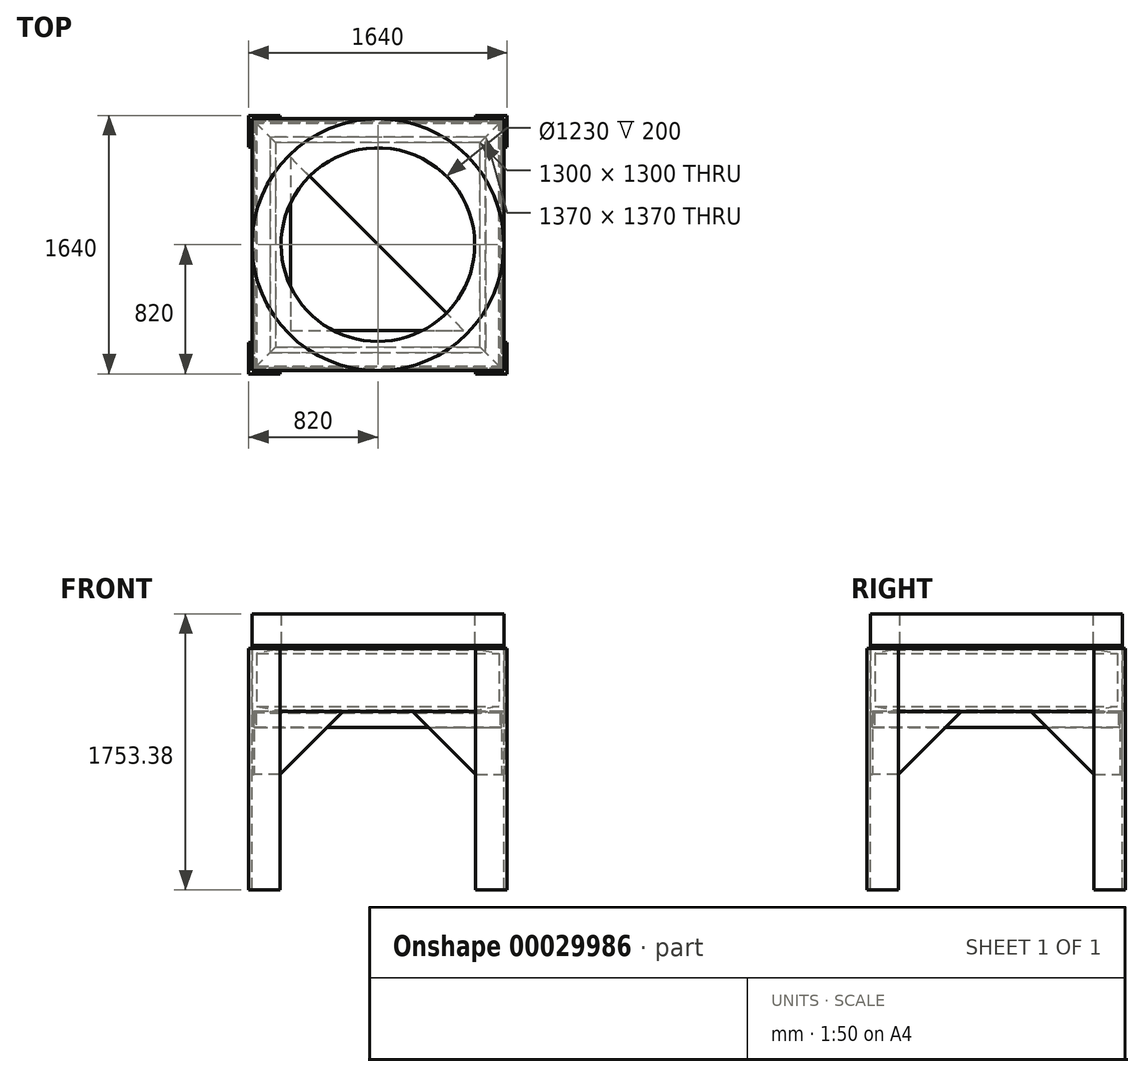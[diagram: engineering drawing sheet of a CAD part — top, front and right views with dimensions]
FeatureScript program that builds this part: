
annotation { "Feature Type Name" : "Feature", "Feature Type Description" : "" }
export const myFeature = defineFeature(function(context is Context, id is Id, definition is map)
    precondition{}
    {
        {
            var Q0;
            Q0=qCreatedBy(makeId("Top.planeOp"),FACE);
            var sketch = newSketch(context, id + "F0", { "sketchPlane" : qUnion([Q0])});
            skLineSegment(sketch, "E0.rect.bottom", {"start": v(800, -800) * mm, "end": v(-800, -800) * mm});
            skLineSegment(sketch, "E0.rect.top", {"start": v(800, 800) * mm, "end": v(-800, 800) * mm});
            skLineSegment(sketch, "E0.rect.left", {"start": v(800, -800) * mm, "end": v(800, 800) * mm});
            skLineSegment(sketch, "E0.rect.right", {"start": v(-800, -800) * mm, "end": v(-800, 800) * mm});
            skPoint(sketch, "E0.rect.middle", {"position": v(0, 0) * mm});
            skSolve(sketch);
        }
        {
            var Q0;
            Q0=qCreatedBy(makeId("Front.planeOp"),FACE);
            var sketch = newSketch(context, id + "F1", { "sketchPlane" : qUnion([Q0])});
            skLineSegment(sketch, "E1", {"start": v(-650, 200) * mm, "end": v(-800, 200) * mm});
            skLineSegment(sketch, "E2", {"start": v(-800, 200) * mm, "end": v(-800, -200) * mm});
            skLineSegment(sketch, "E3", {"start": v(-800, -200) * mm, "end": v(-650, -200) * mm});
            skLineSegment(sketch, "E4", {"start": v(-650, -200) * mm, "end": v(-650, -190) * mm});
            skLineSegment(sketch, "E5", {"start": v(-650, -190) * mm, "end": v(-770, -168.84) * mm});
            skLineSegment(sketch, "E6", {"start": v(-770, -168.84) * mm, "end": v(-770, 168.84) * mm});
            skLineSegment(sketch, "E7", {"start": v(-770, 168.84) * mm, "end": v(-650, 190) * mm});
            skLineSegment(sketch, "E8", {"start": v(-650, 190) * mm, "end": v(-650, 200) * mm});
            skLineSegment(sketch, "E9", {"start": v(0, 0) * mm, "end": v(-1109.35, 0) * mm, "construction": true});
            skSolve(sketch);
        }
        {
            var Q0;
            Q0=makeQuery(id+"F1.imprint","IMPRINT",FACE,{"disambiguationData":[TD([[makeQuery(id+"F1.imprint","IMPRINT",EDGE,{"derivedFrom":sQuery(id+"F1.wireOp",EDGE,"E1")}),1.0]])]});
            var Q1;
            Q1=sQuery(id+"F0.wireOp",EDGE,"E0.rect.right");
            var Q2;
            Q2=sQuery(id+"F0.wireOp",EDGE,"E0.rect.bottom");
            var Q3;
            Q3=sQuery(id+"F0.wireOp",EDGE,"E0.rect.left");
            var Q4;
            Q4=sQuery(id+"F0.wireOp",EDGE,"E0.rect.top");
            sweep(context, id + "F2", {"profiles" : qUnion([Q0]), "path" : qUnion([Q1, Q2, Q3, Q4])});
        }
        {
            var Q0;
            Q0=makeQuery(id+"F2.opSweep","SWEPT_FACE",FACE,{"disambiguationData":[OSD([sQuery(id+"F0.wireOp",EDGE,"E0.rect.right"),sQuery(id+"F1.wireOp",EDGE,"E1")])]});
            var sketch = newSketch(context, id + "F3", { "sketchPlane" : qUnion([Q0])});
            skLineSegment(sketch, "E10", {"start": v(-800, 800) * mm, "end": v(-800, 620) * mm});
            skLineSegment(sketch, "E11", {"start": v(-800, 800) * mm, "end": v(-620, 800) * mm});
            skLineSegment(sketch, "E12", {"start": v(-620, 800) * mm, "end": v(-620, 820) * mm});
            skLineSegment(sketch, "E13", {"start": v(-620, 820) * mm, "end": v(-820, 820) * mm});
            skLineSegment(sketch, "E14", {"start": v(-820, 820) * mm, "end": v(-820, 620) * mm});
            skLineSegment(sketch, "E15", {"start": v(-820, 620) * mm, "end": v(-800, 620) * mm});
            skLineSegment(sketch, "E16", {"start": v(0, 0) * mm, "end": v(0, 1155.08) * mm, "construction": true});
            skLineSegment(sketch, "E17.MirrorCS", {"start": v(800, 800) * mm, "end": v(800, 620) * mm});
            skLineSegment(sketch, "E18.MirrorCS", {"start": v(800, 800) * mm, "end": v(620, 800) * mm});
            skLineSegment(sketch, "E19.MirrorCS", {"start": v(620, 800) * mm, "end": v(620, 820) * mm});
            skLineSegment(sketch, "E20.MirrorCS", {"start": v(620, 820) * mm, "end": v(820, 820) * mm});
            skLineSegment(sketch, "E21.MirrorCS", {"start": v(820, 820) * mm, "end": v(820, 620) * mm});
            skLineSegment(sketch, "E22.MirrorCS", {"start": v(820, 620) * mm, "end": v(800, 620) * mm});
            skSolve(sketch);
        }
        {
            var Q0;
            Q0 = qSketchRegion(id + "F3", true);
            extrude(context, id + "F4", {"entities" : qUnion([Q0]), "oppositeDirection" : true, "depth" : 1533.38 * mm});
        }
        {
            var Q0;
            Q0=makeQuery(id+"F4.opExtrude","SWEPT_BODY",BODY,{"disambiguationData":[OSD([sQuery(id+"F3.wireOp",EDGE,"E17.MirrorCS"),sQuery(id+"F3.wireOp",EDGE,"E18.MirrorCS"),sQuery(id+"F3.wireOp",EDGE,"E19.MirrorCS"),sQuery(id+"F3.wireOp",EDGE,"E20.MirrorCS"),sQuery(id+"F3.wireOp",EDGE,"E21.MirrorCS"),sQuery(id+"F3.wireOp",EDGE,"E22.MirrorCS")])]});
            var Q1;
            Q1=makeQuery(id+"F4.opExtrude","SWEPT_BODY",BODY,{"disambiguationData":[OSD([sQuery(id+"F3.wireOp",EDGE,"E10"),sQuery(id+"F3.wireOp",EDGE,"E11"),sQuery(id+"F3.wireOp",EDGE,"E12"),sQuery(id+"F3.wireOp",EDGE,"E13"),sQuery(id+"F3.wireOp",EDGE,"E14"),sQuery(id+"F3.wireOp",EDGE,"E15")])]});
            var Q2;
            Q2=qCreatedBy(makeId("Front.planeOp"),FACE);
            mirror(context, id + "F5", {"entities" : qUnion([Q0, Q1]), "mirrorPlane" : qUnion([Q2])});
        }
        {
            var Q0;
            Q0=makeQuery(id+"F2.opSweep","SWEPT_FACE",FACE,{"disambiguationData":[OSD([sQuery(id+"F0.wireOp",EDGE,"E0.rect.right"),sQuery(id+"F1.wireOp",EDGE,"E1")])]});
            var sketch = newSketch(context, id + "F6", { "sketchPlane" : qUnion([Q0])});
            skLineSegment(sketch, "E23.bottom", {"start": v(-800, 800) * mm, "end": v(800, 800) * mm});
            skLineSegment(sketch, "E23.top", {"start": v(-800, -800) * mm, "end": v(800, -800) * mm});
            skLineSegment(sketch, "E23.left", {"start": v(-800, 800) * mm, "end": v(-800, -800) * mm});
            skLineSegment(sketch, "E23.right", {"start": v(800, 800) * mm, "end": v(800, -800) * mm});
            skLineSegment(sketch, "E24", {"start": v(-555, 555) * mm, "end": v(-555, -545) * mm});
            skLineSegment(sketch, "E25", {"start": v(-555, -545) * mm, "end": v(545, -545) * mm});
            skLineSegment(sketch, "E26", {"start": v(545, -545) * mm, "end": v(-555, 555) * mm});
            skSolve(sketch);
        }
        {
            var Q0;
            Q0 = qSketchRegion(id + "F6", true);
            extrude(context, id + "F7", {"entities" : qUnion([Q0]), "depth" : 20 * mm});
        }
        {
            var Q0;
            Q0=makeQuery(id+"F7.opExtrude","CAP_FACE",FACE,{"disambiguationData":[OSD([sQuery(id+"F6.wireOp",EDGE,"E23.bottom"),sQuery(id+"F6.wireOp",EDGE,"E23.top"),sQuery(id+"F6.wireOp",EDGE,"E23.left"),sQuery(id+"F6.wireOp",EDGE,"E23.right"),sQuery(id+"F6.wireOp",EDGE,"E24"),sQuery(id+"F6.wireOp",EDGE,"E25"),sQuery(id+"F6.wireOp",EDGE,"E26")])],"isStart":false});
            var sketch = newSketch(context, id + "F8", { "sketchPlane" : qUnion([Q0])});
            skCircle(sketch, "E27", {"center": v(0, 0) * mm, "radius": 800 * mm});
            skCircle(sketch, "E28", {"center": v(0, 0) * mm, "radius": 615 * mm});
            skSolve(sketch);
        }
        {
            var Q0;
            Q0 = qSketchRegion(id + "F8", true);
            extrude(context, id + "F9", {"entities" : qUnion([Q0]), "operationType" : NewBodyOperationType.ADD, "depth" : 200 * mm});
        }
        {
            var Q0;
            Q0=makeQuery(id+"F2.opSweep","SWEPT_FACE",FACE,{"disambiguationData":[OSD([sQuery(id+"F0.wireOp",EDGE,"E0.rect.right"),sQuery(id+"F1.wireOp",EDGE,"E3")])]});
            var sketch = newSketch(context, id + "F10", { "sketchPlane" : qUnion([Q0])});
            skLineSegment(sketch, "E29.rect.bottom", {"start": v(785, -785) * mm, "end": v(-785, -785) * mm});
            skLineSegment(sketch, "E29.rect.top", {"start": v(785, 785) * mm, "end": v(-785, 785) * mm});
            skLineSegment(sketch, "E29.rect.left", {"start": v(785, -785) * mm, "end": v(785, 785) * mm});
            skLineSegment(sketch, "E29.rect.right", {"start": v(-785, -785) * mm, "end": v(-785, 785) * mm});
            skPoint(sketch, "E29.rect.middle", {"position": v(0, 0) * mm});
            skSolve(sketch);
        }
        {
            var Q0;
            Q0=qCreatedBy(makeId("Front.planeOp"),FACE);
            var sketch = newSketch(context, id + "F11", { "sketchPlane" : qUnion([Q0])});
            skLineSegment(sketch, "E30", {"start": v(-785, -300) * mm, "end": v(-785, -200) * mm});
            skLineSegment(sketch, "E31", {"start": v(-785, -200) * mm, "end": v(-685, -200) * mm});
            skLineSegment(sketch, "E32", {"start": v(-685, -200) * mm, "end": v(-685, -210) * mm});
            skLineSegment(sketch, "E33", {"start": v(-685, -210) * mm, "end": v(-775, -210) * mm});
            skLineSegment(sketch, "E34", {"start": v(-775, -210) * mm, "end": v(-775, -300) * mm});
            skLineSegment(sketch, "E35", {"start": v(-775, -300) * mm, "end": v(-785, -300) * mm});
            skSolve(sketch);
        }
        {
            var Q0;
            Q0=makeQuery(id+"F11.imprint","IMPRINT",FACE,{"disambiguationData":[TD([[makeQuery(id+"F11.imprint","IMPRINT",EDGE,{"derivedFrom":sQuery(id+"F11.wireOp",EDGE,"E30")}),-1.0]])]});
            var Q1;
            Q1=sQuery(id+"F10.wireOp",EDGE,"E29.rect.right");
            var Q2;
            Q2=sQuery(id+"F10.wireOp",EDGE,"E29.rect.top");
            var Q3;
            Q3=sQuery(id+"F10.wireOp",EDGE,"E29.rect.left");
            var Q4;
            Q4=sQuery(id+"F10.wireOp",EDGE,"E29.rect.bottom");
            sweep(context, id + "F12", {"profiles" : qUnion([Q0]), "path" : qUnion([Q1, Q2, Q3, Q4])});
        }
        {
            var Q0;
            Q0=makeQuery(id+"F12.opSweep","SWEPT_FACE",FACE,{"disambiguationData":[OSD([sQuery(id+"F10.wireOp",EDGE,"E29.rect.top"),sQuery(id+"F11.wireOp",EDGE,"E30")])]});
            var sketch = newSketch(context, id + "F13", { "sketchPlane" : qUnion([Q0])});
            skLineSegment(sketch, "E36", {"start": v(-800, -200) * mm, "end": v(-220, -200) * mm});
            skLineSegment(sketch, "E37", {"start": v(-220, -200) * mm, "end": v(-620, -600) * mm});
            skLineSegment(sketch, "E38", {"start": v(-800, -600) * mm, "end": v(-800, -200) * mm});
            skPoint(sketch, "E39", {"position": v(-620, -600) * mm});
            skLineSegment(sketch, "E40", {"start": v(-620, -600) * mm, "end": v(-800, -600) * mm});
            skSolve(sketch);
        }
        {
            var Q0;
            Q0 = qSketchRegion(id + "F13", true);
            var Q1;
            Q1=makeQuery(id+"F2.opSweep","SWEPT_FACE",FACE,{"disambiguationData":[OSD([sQuery(id+"F0.wireOp",EDGE,"E0.rect.bottom"),sQuery(id+"F1.wireOp",EDGE,"E2")])]});
            extrude(context, id + "F14", {"entities" : qUnion([Q0]), "endBound" : BoundingType.UP_TO_SURFACE, "endBoundEntityFace" : qUnion([Q1]), "depth" : 25 * mm});
        }
        {
            var Q0;
            Q0=makeQuery(id+"F14.opExtrude","SWEPT_BODY",BODY,{"disambiguationData":[OSD([sQuery(id+"F13.wireOp",EDGE,"E36"),sQuery(id+"F13.wireOp",EDGE,"E37"),sQuery(id+"F13.wireOp",EDGE,"E38"),sQuery(id+"F13.wireOp",EDGE,"E40")])]});
            var Q1;
            Q1=qCreatedBy(makeId("Right.planeOp"),FACE);
            mirror(context, id + "F15", {"entities" : qUnion([Q0]), "mirrorPlane" : qUnion([Q1])});
        }
        {
            var Q0;
            Q0=makeQuery(id+"F14.opExtrude","SWEPT_BODY",BODY,{"disambiguationData":[OSD([sQuery(id+"F13.wireOp",EDGE,"E36"),sQuery(id+"F13.wireOp",EDGE,"E37"),sQuery(id+"F13.wireOp",EDGE,"E38"),sQuery(id+"F13.wireOp",EDGE,"E40")])]});
            var Q1;
            Q1=makeQuery(id+"F15.opPattern","COPY",BODY,{"derivedFrom":makeQuery(id+"F14.opExtrude","SWEPT_BODY",BODY,{"disambiguationData":[OSD([sQuery(id+"F13.wireOp",EDGE,"E36"),sQuery(id+"F13.wireOp",EDGE,"E37"),sQuery(id+"F13.wireOp",EDGE,"E38"),sQuery(id+"F13.wireOp",EDGE,"E40")])]}),"instanceName":"1"});
            var Q2;
            Q2=qCreatedBy(makeId("Front.planeOp"),FACE);
            mirror(context, id + "F16", {"entities" : qUnion([Q0, Q1]), "mirrorPlane" : qUnion([Q2])});
        }
        {
            var Q0;
            Q0=makeQuery(id+"F12.opSweep","SWEPT_FACE",FACE,{"disambiguationData":[OSD([sQuery(id+"F10.wireOp",EDGE,"E29.rect.right"),sQuery(id+"F11.wireOp",EDGE,"E30")])]});
            var sketch = newSketch(context, id + "F17", { "sketchPlane" : qUnion([Q0])});
            skLineSegment(sketch, "E41", {"start": v(-800, -200) * mm, "end": v(-220, -200) * mm});
            skLineSegment(sketch, "E42", {"start": v(-220, -200) * mm, "end": v(-620, -600) * mm});
            skLineSegment(sketch, "E43", {"start": v(-620, -600) * mm, "end": v(-800, -600) * mm});
            skLineSegment(sketch, "E44", {"start": v(-800, -600) * mm, "end": v(-800, -200) * mm});
            skSolve(sketch);
        }
        {
            var Q0;
            Q0 = qSketchRegion(id + "F17", true);
            var Q1;
            Q1=makeQuery(id+"F4.opExtrude","SWEPT_FACE",FACE,{"disambiguationData":[OSD([sQuery(id+"F3.wireOp",EDGE,"E10")])]});
            extrude(context, id + "F18", {"entities" : qUnion([Q0]), "endBound" : BoundingType.UP_TO_SURFACE, "endBoundEntityFace" : qUnion([Q1]), "depth" : 25 * mm});
        }
        {
            var Q0;
            Q0=makeQuery(id+"F18.opExtrude","SWEPT_BODY",BODY,{"disambiguationData":[OSD([sQuery(id+"F17.wireOp",EDGE,"E41"),sQuery(id+"F17.wireOp",EDGE,"E42"),sQuery(id+"F17.wireOp",EDGE,"E43"),sQuery(id+"F17.wireOp",EDGE,"E44")])]});
            var Q1;
            Q1=qCreatedBy(makeId("Front.planeOp"),FACE);
            mirror(context, id + "F19", {"entities" : qUnion([Q0]), "mirrorPlane" : qUnion([Q1])});
        }
        {
            var Q0;
            Q0=makeQuery(id+"F18.opExtrude","SWEPT_BODY",BODY,{"disambiguationData":[OSD([sQuery(id+"F17.wireOp",EDGE,"E41"),sQuery(id+"F17.wireOp",EDGE,"E42"),sQuery(id+"F17.wireOp",EDGE,"E43"),sQuery(id+"F17.wireOp",EDGE,"E44")])]});
            var Q1;
            Q1=makeQuery(id+"F19.opPattern","COPY",BODY,{"derivedFrom":makeQuery(id+"F18.opExtrude","SWEPT_BODY",BODY,{"disambiguationData":[OSD([sQuery(id+"F17.wireOp",EDGE,"E41"),sQuery(id+"F17.wireOp",EDGE,"E42"),sQuery(id+"F17.wireOp",EDGE,"E43"),sQuery(id+"F17.wireOp",EDGE,"E44")])]}),"instanceName":"1"});
            var Q2;
            Q2=qCreatedBy(makeId("Right.planeOp"),FACE);
            mirror(context, id + "F20", {"entities" : qUnion([Q0, Q1]), "mirrorPlane" : qUnion([Q2])});
        }
        {
            var Q0;
            Q0=qCreatedBy(makeId("Right.planeOp"),FACE);
            var sketch = newSketch(context, id + "F21", { "sketchPlane" : qUnion([Q0])});
            skLineSegment(sketch, "E45", {"start": v(0, 0) * mm, "end": v(0, 655.7) * mm, "construction": true});
            skSolve(sketch);
        }
        {
            var Q0;
            Q0=sQuery(id+"F21.wireOp",EDGE,"E45");
            cPlane(context, id + "F22", {"entities" : qUnion([Q0]), "cplaneType" : CPlaneType.LINE_ANGLE, "offset" : 150 * mm, "angle" : 45 * degree, "width" : 150 * mm, "height" : 150 * mm});
        }
    });
